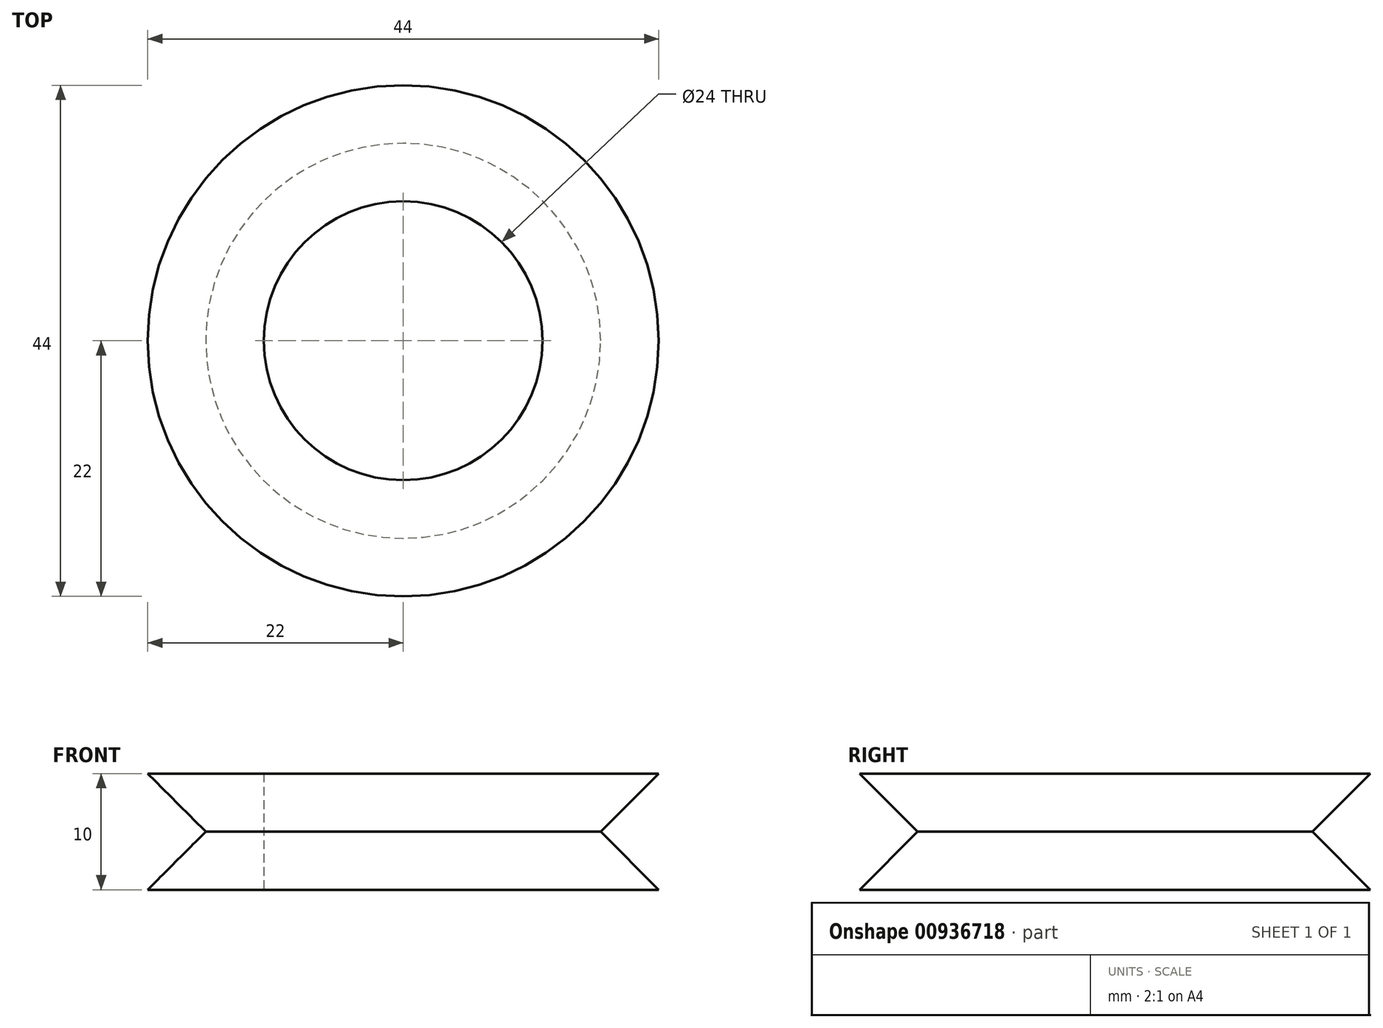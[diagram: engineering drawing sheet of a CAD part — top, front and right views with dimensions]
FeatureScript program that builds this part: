
annotation { "Feature Type Name" : "Feature", "Feature Type Description" : "" }
export const myFeature = defineFeature(function(context is Context, id is Id, definition is map)
    precondition{}
    {
        {
            var Q0;
            Q0=qCreatedBy(makeId("Right.planeOp"),FACE);
            var sketch = newSketch(context, id + "F0", { "sketchPlane" : qUnion([Q0])});
            skLineSegment(sketch, "E0", {"start": v(0, 0) * mm, "end": v(-12, 0) * mm});
            skLineSegment(sketch, "E1", {"start": v(-12, 0) * mm, "end": v(-22, 0) * mm});
            skLineSegment(sketch, "E2", {"start": v(-22, 0) * mm, "end": v(-22, 10) * mm});
            skLineSegment(sketch, "E3", {"start": v(-12, 0) * mm, "end": v(-12, 10) * mm});
            skLineSegment(sketch, "E4", {"start": v(-22, 10) * mm, "end": v(-12, 10) * mm});
            skLineSegment(sketch, "E5", {"start": v(-22, 0) * mm, "end": v(-17, 0) * mm});
            skLineSegment(sketch, "E6", {"start": v(-17, 0) * mm, "end": v(-17, 10) * mm});
            skLineSegment(sketch, "E7", {"start": v(-22, 10) * mm, "end": v(-22, 5) * mm});
            skLineSegment(sketch, "E8", {"start": v(-22, 5) * mm, "end": v(-17, 5) * mm});
            skLineSegment(sketch, "E9", {"start": v(-22, 10) * mm, "end": v(-17, 5) * mm});
            skLineSegment(sketch, "E10", {"start": v(-22, 0) * mm, "end": v(-17, 5) * mm});
            skLineSegment(sketch, "E11", {"start": v(0, 0) * mm, "end": v(0, 15.44) * mm});
            skSolve(sketch);
        }
        {
            var Q0;
            {var subQ3=sQuery(id+"F0.wireOp",EDGE,"E9");Q0=makeQuery(id+"F0.imprint","IMPRINT",FACE,{"disambiguationData":[TD([[makeQuery(id+"F0.imprint","IMPRINT",EDGE,{"derivedFrom":subQ3}),1.0]])]});}
            var Q1;
            {var subQ0=sQuery(id+"F0.wireOp",EDGE,"E10");Q1=makeQuery(id+"F0.imprint","IMPRINT",FACE,{"disambiguationData":[TD([[makeQuery(id+"F0.imprint","IMPRINT",EDGE,{"derivedFrom":subQ0}),-1.0]])]});}
            var Q2;
            {var subQ4=sQuery(id+"F0.wireOp",EDGE,"E3");Q2=makeQuery(id+"F0.imprint","IMPRINT",FACE,{"disambiguationData":[TD([[makeQuery(id+"F0.imprint","IMPRINT",EDGE,{"derivedFrom":subQ4}),1.0]])]});}
            var Q3;
            Q3=sQuery(id+"F0.wireOp",EDGE,"E11");
            revolve(context, id + "F1", {"surfaceOperationType" : NewSurfaceOperationType.NEW, "entities" : qUnion([Q0, Q1, Q2]), "axis" : qUnion([Q3]), "revolveType" : RevolveType.FULL});
        }
    });
